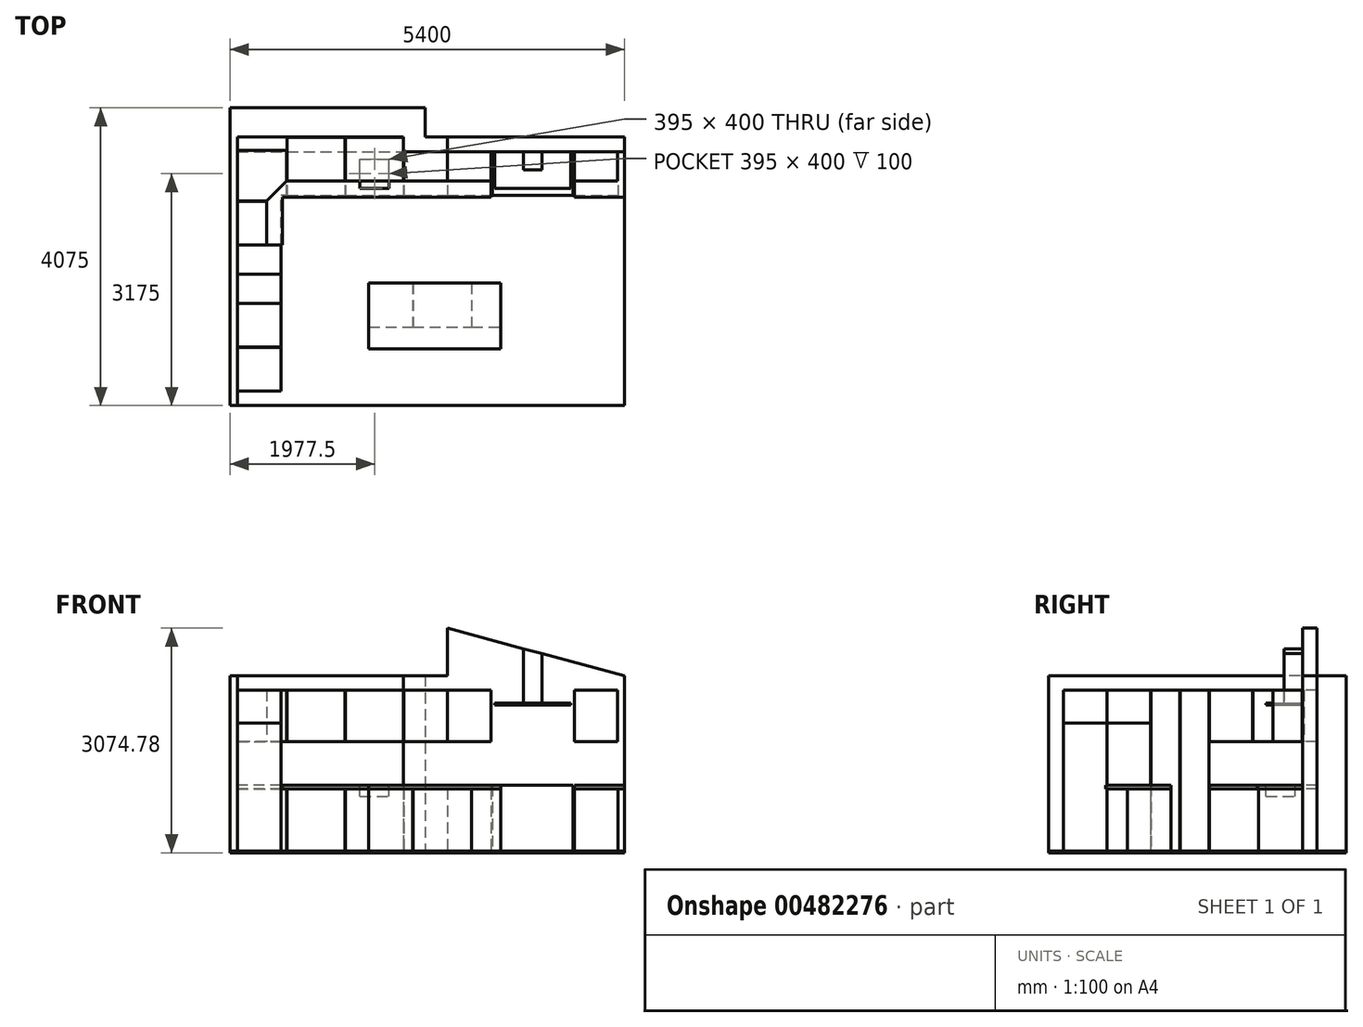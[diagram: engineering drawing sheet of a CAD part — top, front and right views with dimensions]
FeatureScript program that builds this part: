
annotation { "Feature Type Name" : "Feature", "Feature Type Description" : "" }
export const myFeature = defineFeature(function(context is Context, id is Id, definition is map)
    precondition{}
    {
        {
            var Q0;
            Q0=qCreatedBy(makeId("Top.planeOp"),FACE);
            var sketch = newSketch(context, id + "F0", { "sketchPlane" : qUnion([Q0])});
            skLineSegment(sketch, "E0", {"start": v(0, 200) * mm, "end": v(0, -3475) * mm});
            skLineSegment(sketch, "E1", {"start": v(0, 200) * mm, "end": v(2275, 200) * mm});
            skLineSegment(sketch, "E2", {"start": v(2275, 200) * mm, "end": v(2275, 0) * mm});
            skLineSegment(sketch, "E3", {"start": v(2275, 0) * mm, "end": v(5300, 0) * mm});
            skLineSegment(sketch, "E4", {"start": v(0, -3475) * mm, "end": v(-100, -3475) * mm});
            skLineSegment(sketch, "E5", {"start": v(-100, -3475) * mm, "end": v(-100, 600) * mm});
            skLineSegment(sketch, "E6", {"start": v(-100, 600) * mm, "end": v(2575, 600) * mm});
            skLineSegment(sketch, "E7", {"start": v(2575, 600) * mm, "end": v(2575, 200) * mm});
            skLineSegment(sketch, "E8", {"start": v(2575, 200) * mm, "end": v(5300, 200) * mm});
            skLineSegment(sketch, "E9", {"start": v(5300, 200) * mm, "end": v(5300, 0) * mm});
            skLineSegment(sketch, "E10", {"start": v(0, -3475) * mm, "end": v(5300, -3475) * mm});
            skLineSegment(sketch, "E11", {"start": v(5300, -3475) * mm, "end": v(5300, 0) * mm});
            skSolve(sketch);
        }
        {
            var Q0;
            Q0=makeQuery(id+"F0.imprint","IMPRINT",FACE,{"disambiguationData":[TD([[makeQuery(id+"F0.imprint","IMPRINT",EDGE,{"derivedFrom":sQuery(id+"F0.wireOp",EDGE,"E0")}),-1.0]])]});
            extrude(context, id + "F1", {"entities" : qUnion([Q0]), "depth" : 2400 * mm});
        }
        {
            var Q0;
            Q0=qCreatedBy(makeId("Top.planeOp"),FACE);
            var sketch = newSketch(context, id + "F2", { "sketchPlane" : qUnion([Q0])});
            skLineSegment(sketch, "E12", {"start": v(0, 0) * mm, "end": v(675, 0) * mm});
            skLineSegment(sketch, "E13", {"start": v(675, -600) * mm, "end": v(675, 0) * mm});
            skLineSegment(sketch, "E14", {"start": v(675, -600) * mm, "end": v(600, -600) * mm});
            skLineSegment(sketch, "E15", {"start": v(600, -1275) * mm, "end": v(600, -600) * mm});
            skLineSegment(sketch, "E16", {"start": v(600, -1275) * mm, "end": v(0, -1275) * mm});
            skLineSegment(sketch, "E17", {"start": v(0, 0) * mm, "end": v(0, -1275) * mm});
            skLineSegment(sketch, "E18.bottom", {"start": v(680, 0) * mm, "end": v(1475, 0) * mm});
            skLineSegment(sketch, "E18.top", {"start": v(680, -600) * mm, "end": v(1475, -600) * mm});
            skLineSegment(sketch, "E18.left", {"start": v(680, 0) * mm, "end": v(680, -600) * mm});
            skLineSegment(sketch, "E18.right", {"start": v(1475, 0) * mm, "end": v(1475, -600) * mm});
            skLineSegment(sketch, "E19.bottom", {"start": v(1480, 0) * mm, "end": v(2275, 0) * mm});
            skLineSegment(sketch, "E19.top", {"start": v(1480, -600) * mm, "end": v(2275, -600) * mm});
            skLineSegment(sketch, "E19.left", {"start": v(1480, 0) * mm, "end": v(1480, -600) * mm});
            skLineSegment(sketch, "E19.right", {"start": v(2275, 0) * mm, "end": v(2275, -600) * mm});
            skLineSegment(sketch, "E20.bottom", {"start": v(2280, 0) * mm, "end": v(2875, 0) * mm});
            skLineSegment(sketch, "E20.top", {"start": v(2280, -600) * mm, "end": v(2875, -600) * mm});
            skLineSegment(sketch, "E20.left", {"start": v(2280, 0) * mm, "end": v(2280, -600) * mm});
            skLineSegment(sketch, "E20.right", {"start": v(2875, 0) * mm, "end": v(2875, -600) * mm});
            skLineSegment(sketch, "E21.bottom", {"start": v(2880, 0) * mm, "end": v(3475, 0) * mm});
            skLineSegment(sketch, "E21.top", {"start": v(2880, -600) * mm, "end": v(3475, -600) * mm});
            skLineSegment(sketch, "E21.left", {"start": v(2880, 0) * mm, "end": v(2880, -600) * mm});
            skLineSegment(sketch, "E21.right", {"start": v(3475, 0) * mm, "end": v(3475, -600) * mm});
            skLineSegment(sketch, "E22.bottom", {"start": v(3495, 0) * mm, "end": v(4595, 0) * mm});
            skLineSegment(sketch, "E22.top", {"start": v(3495, -600) * mm, "end": v(4595, -600) * mm});
            skLineSegment(sketch, "E22.left", {"start": v(3495, 0) * mm, "end": v(3495, -600) * mm});
            skLineSegment(sketch, "E22.right", {"start": v(4595, 0) * mm, "end": v(4595, -600) * mm});
            skLineSegment(sketch, "E23.bottom", {"start": v(4615, 0) * mm, "end": v(5215, 0) * mm});
            skLineSegment(sketch, "E23.top", {"start": v(4615, -600) * mm, "end": v(5215, -600) * mm});
            skLineSegment(sketch, "E23.left", {"start": v(4615, 0) * mm, "end": v(4615, -600) * mm});
            skLineSegment(sketch, "E23.right", {"start": v(5215, 0) * mm, "end": v(5215, -600) * mm});
            skSolve(sketch);
        }
        {
            var Q0;
            Q0=makeQuery(id+"F2.imprint","IMPRINT",FACE,{"disambiguationData":[TD([[makeQuery(id+"F2.imprint","IMPRINT",EDGE,{"derivedFrom":sQuery(id+"F2.wireOp",EDGE,"E12")}),1.0]])]});
            var Q1;
            Q1=makeQuery(id+"F2.imprint","IMPRINT",FACE,{"disambiguationData":[TD([[makeQuery(id+"F2.imprint","IMPRINT",EDGE,{"derivedFrom":sQuery(id+"F2.wireOp",EDGE,"E12")}),-1.0]])]});
            extrude(context, id + "F3", {"entities" : qUnion([Q0, Q1]), "depth" : 850 * mm});
        }
        {
            var Q0;
            Q0=qCreatedBy(makeId("Top.planeOp"),FACE);
            var sketch = newSketch(context, id + "F4", { "sketchPlane" : qUnion([Q0])});
            skLineSegment(sketch, "E24.bottom", {"start": v(0, -1280) * mm, "end": v(600, -1280) * mm});
            skLineSegment(sketch, "E24.top", {"start": v(0, -2075) * mm, "end": v(600, -2075) * mm});
            skLineSegment(sketch, "E24.left", {"start": v(0, -1280) * mm, "end": v(0, -1675) * mm});
            skLineSegment(sketch, "E24.right", {"start": v(600, -1280) * mm, "end": v(600, -1675) * mm});
            skLineSegment(sketch, "E25.bottom", {"start": v(0, -2080) * mm, "end": v(600, -2080) * mm});
            skLineSegment(sketch, "E25.top", {"start": v(0, -2675) * mm, "end": v(600, -2675) * mm});
            skLineSegment(sketch, "E25.left", {"start": v(0, -2080) * mm, "end": v(0, -2675) * mm});
            skLineSegment(sketch, "E25.right", {"start": v(600, -2080) * mm, "end": v(600, -2675) * mm});
            skLineSegment(sketch, "E26.bottom", {"start": v(0, -2680) * mm, "end": v(600, -2680) * mm});
            skLineSegment(sketch, "E26.top", {"start": v(0, -3275) * mm, "end": v(600, -3275) * mm});
            skLineSegment(sketch, "E26.left", {"start": v(0, -2680) * mm, "end": v(0, -3275) * mm});
            skLineSegment(sketch, "E26.right", {"start": v(600, -2680) * mm, "end": v(600, -3275) * mm});
            skLineSegment(sketch, "E27", {"start": v(0, -1680) * mm, "end": v(600, -1680) * mm});
            skPoint(sketch, "E27.endSnap0", {"position": v(600, -1677.5) * mm});
            skLineSegment(sketch, "E28", {"start": v(0, -1675) * mm, "end": v(600, -1675) * mm});
            skLineSegment(sketch, "E29.trimOffspring", {"start": v(0, -1680) * mm, "end": v(0, -2075) * mm});
            skLineSegment(sketch, "E30.trimOffspring", {"start": v(600, -1680) * mm, "end": v(600, -2075) * mm});
            skSolve(sketch);
        }
        {
            var Q0;
            Q0=makeQuery(id+"F4.imprint","IMPRINT",FACE,{"disambiguationData":[TD([[makeQuery(id+"F4.imprint","IMPRINT",EDGE,{"derivedFrom":sQuery(id+"F4.wireOp",EDGE,"xJVdDzhz-qRA4-ksoh-fODy-tzABdkis1T4j.bottom")}),-1.0]])]});
            var Q1;
            Q1=makeQuery(id+"F4.imprint","IMPRINT",FACE,{"disambiguationData":[TD([[makeQuery(id+"F4.imprint","IMPRINT",EDGE,{"derivedFrom":sQuery(id+"F4.wireOp",EDGE,"E24.bottom")}),-1.0]])]});
            extrude(context, id + "F5", {"entities" : qUnion([Q0, Q1]), "depth" : 2200 * mm});
        }
        {
            var Q0;
            Q0=makeQuery(id+"F4.imprint","IMPRINT",FACE,{"disambiguationData":[TD([[makeQuery(id+"F4.imprint","IMPRINT",EDGE,{"derivedFrom":sQuery(id+"F4.wireOp",EDGE,"E24.top")}),1.0]])]});
            extrude(context, id + "F6", {"entities" : qUnion([Q0]), "depth" : 2200 * mm});
        }
        {
            var Q0;
            Q0=makeQuery(id+"F4.imprint","IMPRINT",FACE,{"disambiguationData":[TD([[makeQuery(id+"F4.imprint","IMPRINT",EDGE,{"derivedFrom":sQuery(id+"F4.wireOp",EDGE,"E25.bottom")}),-1.0]])]});
            extrude(context, id + "F7", {"entities" : qUnion([Q0]), "depth" : 1750 * mm});
        }
        {
            var Q0;
            Q0=makeQuery(id+"F4.imprint","IMPRINT",FACE,{"disambiguationData":[TD([[makeQuery(id+"F4.imprint","IMPRINT",EDGE,{"derivedFrom":sQuery(id+"F4.wireOp",EDGE,"E26.bottom")}),-1.0]])]});
            extrude(context, id + "F8", {"entities" : qUnion([Q0]), "depth" : 1750 * mm});
        }
        {
            var Q0;
            Q0=makeQuery(id+"F2.imprint","IMPRINT",FACE,{"disambiguationData":[TD([[makeQuery(id+"F2.imprint","IMPRINT",EDGE,{"derivedFrom":sQuery(id+"F2.wireOp",EDGE,"E18.bottom")}),-1.0]])]});
            extrude(context, id + "F9", {"entities" : qUnion([Q0]), "depth" : 850 * mm});
        }
        {
            var Q0;
            Q0=makeQuery(id+"F2.imprint","IMPRINT",FACE,{"disambiguationData":[TD([[makeQuery(id+"F2.imprint","IMPRINT",EDGE,{"derivedFrom":sQuery(id+"F2.wireOp",EDGE,"E19.bottom")}),-1.0]])]});
            extrude(context, id + "F10", {"entities" : qUnion([Q0]), "depth" : 850 * mm});
        }
        {
            var Q0;
            Q0=makeQuery(id+"F2.imprint","IMPRINT",FACE,{"disambiguationData":[TD([[makeQuery(id+"F2.imprint","IMPRINT",EDGE,{"derivedFrom":sQuery(id+"F2.wireOp",EDGE,"E20.bottom")}),-1.0]])]});
            extrude(context, id + "F11", {"entities" : qUnion([Q0]), "depth" : 850 * mm});
        }
        {
            var Q0;
            Q0=makeQuery(id+"F2.imprint","IMPRINT",FACE,{"disambiguationData":[TD([[makeQuery(id+"F2.imprint","IMPRINT",EDGE,{"derivedFrom":sQuery(id+"F2.wireOp",EDGE,"E21.bottom")}),-1.0]])]});
            extrude(context, id + "F12", {"entities" : qUnion([Q0]), "depth" : 850 * mm});
        }
        {
            var Q0;
            Q0=makeQuery(id+"F2.imprint","IMPRINT",FACE,{"disambiguationData":[TD([[makeQuery(id+"F2.imprint","IMPRINT",EDGE,{"derivedFrom":sQuery(id+"F2.wireOp",EDGE,"E22.bottom")}),-1.0]])]});
            extrude(context, id + "F13", {"entities" : qUnion([Q0]), "depth" : 900 * mm});
        }
        {
            var Q0;
            Q0=makeQuery(id+"F2.imprint","IMPRINT",FACE,{"disambiguationData":[TD([[makeQuery(id+"F2.imprint","IMPRINT",EDGE,{"derivedFrom":sQuery(id+"F2.wireOp",EDGE,"E23.bottom")}),-1.0]])]});
            extrude(context, id + "F14", {"entities" : qUnion([Q0]), "depth" : 850 * mm});
        }
        {
            var Q0;
            Q0=qCreatedBy(makeId("Top.planeOp"),FACE);
            cPlane(context, id + "F15", {"entities" : qUnion([Q0]), "cplaneType" : CPlaneType.OFFSET, "offset" : 1500 * mm, "width" : 150 * mm, "height" : 150 * mm});
        }
        {
            var Q0;
            Q0=qCreatedBy(id+"F15.planeOp",FACE);
            var sketch = newSketch(context, id + "F16", { "sketchPlane" : qUnion([Q0])});
            skLineSegment(sketch, "E31.bottom", {"start": v(1, 199) * mm, "end": v(675, 199) * mm});
            skLineSegment(sketch, "E31.left", {"start": v(1, 199) * mm, "end": v(1, -676) * mm});
            skLineSegment(sketch, "E31.right", {"start": v(675, 199) * mm, "end": v(675, -401) * mm});
            skPoint(sketch, "E32.0", {"position": v(0, 200) * mm});
            skLineSegment(sketch, "E33.bottom", {"start": v(680, 199) * mm, "end": v(1475, 199) * mm});
            skLineSegment(sketch, "E33.top", {"start": v(680, -401) * mm, "end": v(1475, -401) * mm});
            skLineSegment(sketch, "E33.left", {"start": v(680, 199) * mm, "end": v(680, -401) * mm});
            skLineSegment(sketch, "E33.right", {"start": v(1475, 199) * mm, "end": v(1475, -401) * mm});
            skLineSegment(sketch, "E34.bottom", {"start": v(1480, 199) * mm, "end": v(2275, 199) * mm});
            skLineSegment(sketch, "E34.top", {"start": v(1480, -401) * mm, "end": v(2275, -401) * mm});
            skLineSegment(sketch, "E34.left", {"start": v(1480, 199) * mm, "end": v(1480, -401) * mm});
            skLineSegment(sketch, "E34.right", {"start": v(2275, 199) * mm, "end": v(2275, -401) * mm});
            skLineSegment(sketch, "E35.bottom", {"start": v(2280, -401) * mm, "end": v(2875, -401) * mm});
            skLineSegment(sketch, "E35.top", {"start": v(2280, -1) * mm, "end": v(2875, -1) * mm});
            skLineSegment(sketch, "E35.left", {"start": v(2280, -401) * mm, "end": v(2280, -1) * mm});
            skLineSegment(sketch, "E35.right", {"start": v(2875, -401) * mm, "end": v(2875, -1) * mm});
            skLineSegment(sketch, "E36.bottom", {"start": v(2880, -401) * mm, "end": v(3475, -401) * mm});
            skLineSegment(sketch, "E36.top", {"start": v(2880, -1) * mm, "end": v(3475, -1) * mm});
            skLineSegment(sketch, "E36.left", {"start": v(2880, -401) * mm, "end": v(2880, -1) * mm});
            skLineSegment(sketch, "E36.right", {"start": v(3475, -401) * mm, "end": v(3475, -1) * mm});
            skLineSegment(sketch, "E37.bottom", {"start": v(4615, -401) * mm, "end": v(5210, -401) * mm});
            skLineSegment(sketch, "E37.top", {"start": v(4615, -1) * mm, "end": v(5210, -1) * mm});
            skLineSegment(sketch, "E37.left", {"start": v(4615, -401) * mm, "end": v(4615, -1) * mm});
            skLineSegment(sketch, "E37.right", {"start": v(5210, -401) * mm, "end": v(5210, -1) * mm});
            skLineSegment(sketch, "E38", {"start": v(675, -401) * mm, "end": v(401, -676) * mm});
            skLineSegment(sketch, "E39", {"start": v(401, -676) * mm, "end": v(1, -676) * mm});
            skLineSegment(sketch, "E40.bottom", {"start": v(1, -681) * mm, "end": v(401, -681) * mm});
            skLineSegment(sketch, "E40.top", {"start": v(1, -1276) * mm, "end": v(401, -1276) * mm});
            skLineSegment(sketch, "E40.left", {"start": v(1, -681) * mm, "end": v(1, -1276) * mm});
            skLineSegment(sketch, "E40.right", {"start": v(401, -681) * mm, "end": v(401, -1276) * mm});
            skLineSegment(sketch, "E41", {"start": v(1, 18.87) * mm, "end": v(675, 18.87) * mm});
            skSolve(sketch);
        }
        {
            var Q0;
            Q0=makeQuery(id+"F16.imprint","IMPRINT",FACE,{"disambiguationData":[TD([[makeQuery(id+"F16.imprint","IMPRINT",EDGE,{"derivedFrom":sQuery(id+"F16.wireOp",EDGE,"E33.bottom")}),-1.0]])]});
            extrude(context, id + "F17", {"entities" : qUnion([Q0]), "depth" : 700 * mm});
        }
        {
            var Q0;
            Q0=makeQuery(id+"F16.imprint","IMPRINT",FACE,{"disambiguationData":[TD([[makeQuery(id+"F16.imprint","IMPRINT",EDGE,{"derivedFrom":sQuery(id+"F16.wireOp",EDGE,"E34.bottom")}),-1.0]])]});
            extrude(context, id + "F18", {"entities" : qUnion([Q0]), "depth" : 700 * mm});
        }
        {
            var Q0;
            Q0=makeQuery(id+"F0.imprint","IMPRINT",FACE,{"disambiguationData":[TD([[makeQuery(id+"F0.imprint","IMPRINT",EDGE,{"derivedFrom":sQuery(id+"F0.wireOp",EDGE,"E0")}),-1.0]])]});
            var Q1;
            Q1=makeQuery(id+"F0.imprint","IMPRINT",FACE,{"disambiguationData":[TD([[makeQuery(id+"F0.imprint","IMPRINT",EDGE,{"derivedFrom":sQuery(id+"F0.wireOp",EDGE,"E0")}),1.0]])]});
            extrude(context, id + "F19", {"entities" : qUnion([Q0, Q1]), "oppositeDirection" : true, "depth" : 25 * mm});
        }
        {
            var Q0;
            Q0=makeQuery(id+"F16.imprint","IMPRINT",FACE,{"disambiguationData":[TD([[makeQuery(id+"F16.imprint","IMPRINT",EDGE,{"derivedFrom":sQuery(id+"F16.wireOp",EDGE,"E35.bottom")}),1.0]])]});
            var Q1;
            Q1=makeQuery(id+"F16.imprint","IMPRINT",FACE,{"disambiguationData":[TD([[makeQuery(id+"F16.imprint","IMPRINT",EDGE,{"derivedFrom":sQuery(id+"F16.wireOp",EDGE,"E36.bottom")}),1.0]])]});
            var Q2;
            Q2=makeQuery(id+"F16.imprint","IMPRINT",FACE,{"disambiguationData":[TD([[makeQuery(id+"F16.imprint","IMPRINT",EDGE,{"derivedFrom":sQuery(id+"F16.wireOp",EDGE,"E37.bottom")}),1.0]])]});
            extrude(context, id + "F20", {"entities" : qUnion([Q0, Q1, Q2]), "depth" : 700 * mm});
        }
        {
            var Q0;
            Q0=makeQuery(id+"F1.opExtrude","SWEPT_FACE",FACE,{"disambiguationData":[OSD([sQuery(id+"F0.wireOp",EDGE,"E3")])]});
            var sketch = newSketch(context, id + "F21", { "sketchPlane" : qUnion([Q0])});
            skLineSegment(sketch, "E42", {"start": v(5300, 2400) * mm, "end": v(2875, 3049.78) * mm});
            skLineSegment(sketch, "E43", {"start": v(2875, 3049.78) * mm, "end": v(2875, 2400) * mm});
            skLineSegment(sketch, "E44", {"start": v(2875, 2400) * mm, "end": v(5300, 2400) * mm});
            skLineSegment(sketch, "E45.0", {"start": v(2575, 2400) * mm, "end": v(2575, 0) * mm});
            skSolve(sketch);
        }
        {
            var Q0;
            Q0=makeQuery(id+"F21.imprint","IMPRINT",FACE,{"disambiguationData":[TD([[makeQuery(id+"F21.imprint","IMPRINT",EDGE,{"derivedFrom":sQuery(id+"F21.wireOp",EDGE,"E42")}),1.0]])]});
            extrude(context, id + "F22", {"entities" : qUnion([Q0]), "operationType" : NewBodyOperationType.ADD, "oppositeDirection" : true, "depth" : 200 * mm});
        }
        {
            var Q0;
            Q0=makeQuery(id+"F22.boolean.opBoolean","MERGE",FACE,{"derivedFrom":[makeQuery(id+"F1.opExtrude","SWEPT_FACE",FACE,{"disambiguationData":[OSD([sQuery(id+"F0.wireOp",EDGE,"E3")])]}),makeQuery(id+"F22.opExtrude","CAP_FACE",FACE,{"disambiguationData":[OSD([sQuery(id+"F21.wireOp",EDGE,"E42"),sQuery(id+"F21.wireOp",EDGE,"E43"),sQuery(id+"F21.wireOp",EDGE,"E44")])],"isStart":true})]});
            var sketch = newSketch(context, id + "F23", { "sketchPlane" : qUnion([Q0])});
            skLineSegment(sketch, "E46.bottom", {"start": v(3525, 2000) * mm, "end": v(4565, 2000) * mm});
            skLineSegment(sketch, "E46.top", {"start": v(3525, 2025) * mm, "end": v(3920, 2025) * mm});
            skLineSegment(sketch, "E46.left", {"start": v(3525, 2000) * mm, "end": v(3525, 2025) * mm});
            skLineSegment(sketch, "E46.right", {"start": v(4565, 2000) * mm, "end": v(4565, 2025) * mm});
            skLineSegment(sketch, "E47", {"start": v(3920, 2025) * mm, "end": v(3920, 2769.77) * mm});
            skLineSegment(sketch, "E48", {"start": v(3920, 2769.77) * mm, "end": v(4170, 2702.78) * mm});
            skLineSegment(sketch, "E49", {"start": v(4170, 2702.78) * mm, "end": v(4170, 2025) * mm});
            skLineSegment(sketch, "E50.trimOffspring", {"start": v(4170, 2025) * mm, "end": v(4565, 2025) * mm});
            skLineSegment(sketch, "E51", {"start": v(3920, 2025) * mm, "end": v(4170, 2025) * mm});
            skSolve(sketch);
        }
        {
            var Q0;
            Q0=makeQuery(id+"F23.imprint","IMPRINT",FACE,{"disambiguationData":[TD([[makeQuery(id+"F23.imprint","IMPRINT",EDGE,{"derivedFrom":sQuery(id+"F23.wireOp",EDGE,"E47")}),-1.0]])]});
            extrude(context, id + "F24", {"entities" : qUnion([Q0]), "depth" : 250 * mm});
        }
        {
            var Q0;
            Q0=makeQuery(id+"F23.imprint","IMPRINT",FACE,{"disambiguationData":[TD([[makeQuery(id+"F23.imprint","IMPRINT",EDGE,{"derivedFrom":sQuery(id+"F23.wireOp",EDGE,"E46.bottom")}),1.0]])]});
            extrude(context, id + "F25", {"entities" : qUnion([Q0]), "depth" : 500 * mm});
        }
        {
            var Q0;
            {var subQ1=sQuery(id+"F16.wireOp",EDGE,"E38");Q0=makeQuery(id+"F16.imprint","IMPRINT",FACE,{"disambiguationData":[TD([[makeQuery(id+"F16.imprint","IMPRINT",EDGE,{"derivedFrom":subQ1}),-1.0]])]});}
            extrude(context, id + "F26", {"entities" : qUnion([Q0]), "depth" : 700 * mm});
        }
        {
            var Q0;
            Q0=makeQuery(id+"F16.imprint","IMPRINT",FACE,{"disambiguationData":[TD([[makeQuery(id+"F16.imprint","IMPRINT",EDGE,{"derivedFrom":sQuery(id+"F16.wireOp",EDGE,"E40.bottom")}),-1.0]])]});
            extrude(context, id + "F27", {"entities" : qUnion([Q0]), "depth" : 700 * mm});
        }
        {
            var Q0;
            Q0=makeQuery(id+"F10.opExtrude","CAP_FACE",FACE,{"disambiguationData":[OSD([sQuery(id+"F2.wireOp",EDGE,"E19.bottom"),sQuery(id+"F2.wireOp",EDGE,"E19.top"),sQuery(id+"F2.wireOp",EDGE,"E19.left"),sQuery(id+"F2.wireOp",EDGE,"E19.right")])],"isStart":false});
            var sketch = newSketch(context, id + "F28", { "sketchPlane" : qUnion([Q0])});
            skLineSegment(sketch, "E52.bottom", {"start": v(1680, -500) * mm, "end": v(2075, -500) * mm});
            skLineSegment(sketch, "E52.top", {"start": v(1680, -100) * mm, "end": v(2075, -100) * mm});
            skLineSegment(sketch, "E52.left", {"start": v(1680, -500) * mm, "end": v(1680, -100) * mm});
            skLineSegment(sketch, "E52.right", {"start": v(2075, -500) * mm, "end": v(2075, -100) * mm});
            skSolve(sketch);
        }
        {
            var Q0;
            Q0=makeQuery(id+"F19.opExtrude","CAP_FACE",FACE,{"disambiguationData":[OSD([sQuery(id+"F0.wireOp",EDGE,"E4"),sQuery(id+"F0.wireOp",EDGE,"E5"),sQuery(id+"F0.wireOp",EDGE,"E6"),sQuery(id+"F0.wireOp",EDGE,"E7"),sQuery(id+"F0.wireOp",EDGE,"E8"),sQuery(id+"F0.wireOp",EDGE,"E9"),sQuery(id+"F0.wireOp",EDGE,"E10"),sQuery(id+"F0.wireOp",EDGE,"E11")])],"isStart":true});
            cPlane(context, id + "F29", {"entities" : qUnion([Q0]), "cplaneType" : CPlaneType.OFFSET, "offset" : 851 * mm, "width" : 150 * mm, "height" : 150 * mm});
        }
        {
            var Q0;
            Q0=qCreatedBy(id+"F29.planeOp",FACE);
            var sketch = newSketch(context, id + "F30", { "sketchPlane" : qUnion([Q0])});
            skLineSegment(sketch, "E53.1", {"start": v(0, 200) * mm, "end": v(0, -1274) * mm});
            skLineSegment(sketch, "E53.2", {"start": v(0, 200) * mm, "end": v(2275, 200) * mm});
            skLineSegment(sketch, "E53.3", {"start": v(2275, 200) * mm, "end": v(2275, 0) * mm});
            skLineSegment(sketch, "E53.4", {"start": v(2275, 0) * mm, "end": v(3475, 0) * mm});
            skLineSegment(sketch, "E54.0", {"start": v(5300, 0) * mm, "end": v(5300, -620) * mm});
            skPoint(sketch, "E55.orphan", {"position": v(2875, 0) * mm});
            skPoint(sketch, "E56.orphan", {"position": v(5300, 200) * mm});
            skLineSegment(sketch, "E57", {"start": v(5300, -620) * mm, "end": v(4615, -620) * mm});
            skLineSegment(sketch, "E58", {"start": v(620, -620) * mm, "end": v(620, -1274) * mm});
            skLineSegment(sketch, "E59", {"start": v(620, -1274) * mm, "end": v(0, -1274) * mm});
            skPoint(sketch, "E60.orphan", {"position": v(0, -3475) * mm});
            skPoint(sketch, "E61.orphan", {"position": v(5300, -3475) * mm});
            skLineSegment(sketch, "E62.0", {"start": v(3475, 0) * mm, "end": v(3475, -620) * mm});
            skLineSegment(sketch, "E63.0", {"start": v(4615, 0) * mm, "end": v(4615, -620) * mm});
            skPoint(sketch, "E64.orphan", {"position": v(4615, -600) * mm});
            skPoint(sketch, "E65.orphan", {"position": v(3475, -600) * mm});
            skLineSegment(sketch, "E66.trimOffspring", {"start": v(3475, -620) * mm, "end": v(620, -620) * mm});
            skLineSegment(sketch, "E67.trimOffspring", {"start": v(4615, 0) * mm, "end": v(5300, 0) * mm});
            skSolve(sketch);
        }
        {
            var Q0;
            Q0=makeQuery(id+"F30.imprint","IMPRINT",FACE,{"disambiguationData":[TD([[makeQuery(id+"F30.imprint","IMPRINT",EDGE,{"derivedFrom":sQuery(id+"F30.wireOp",EDGE,"E53.1")}),1.0]])]});
            var Q1;
            Q1=makeQuery(id+"F30.imprint","IMPRINT",FACE,{"disambiguationData":[TD([[makeQuery(id+"F30.imprint","IMPRINT",EDGE,{"derivedFrom":sQuery(id+"F30.wireOp",EDGE,"E54.0")}),-1.0]])]});
            extrude(context, id + "F31", {"entities" : qUnion([Q0, Q1]), "depth" : 50 * mm});
        }
        {
            var Q0;
            Q0=makeQuery(id+"F28.imprint","IMPRINT",FACE,{"disambiguationData":[TD([[makeQuery(id+"F28.imprint","IMPRINT",EDGE,{"derivedFrom":sQuery(id+"F28.wireOp",EDGE,"E52.bottom")}),1.0]])]});
            extrude(context, id + "F32", {"entities" : qUnion([Q0]), "operationType" : NewBodyOperationType.REMOVE, "endBound" : BoundingType.SYMMETRIC, "oppositeDirection" : true, "depth" : 200 * mm});
        }
        {
            var Q0;
            Q0=makeQuery(id+"F5.opExtrude","CAP_FACE",FACE,{"disambiguationData":[OSD([sQuery(id+"F4.wireOp",EDGE,"E24.bottom"),sQuery(id+"F4.wireOp",EDGE,"E24.top"),sQuery(id+"F4.wireOp",EDGE,"E24.left"),sQuery(id+"F4.wireOp",EDGE,"E24.right")])],"isStart":false});
            var sketch = newSketch(context, id + "F33", { "sketchPlane" : qUnion([Q0])});
            skLineSegment(sketch, "E68.bottom", {"start": v(0, -2080) * mm, "end": v(600, -2080) * mm});
            skLineSegment(sketch, "E68.top", {"start": v(0, -2675) * mm, "end": v(600, -2675) * mm});
            skLineSegment(sketch, "E68.left", {"start": v(0, -2080) * mm, "end": v(0, -2675) * mm});
            skLineSegment(sketch, "E68.right", {"start": v(600, -2080) * mm, "end": v(600, -2675) * mm});
            skLineSegment(sketch, "E69.bottom", {"start": v(0, -2680) * mm, "end": v(600, -2680) * mm});
            skLineSegment(sketch, "E69.top", {"start": v(0, -3275) * mm, "end": v(600, -3275) * mm});
            skLineSegment(sketch, "E69.left", {"start": v(0, -2680) * mm, "end": v(0, -3275) * mm});
            skLineSegment(sketch, "E69.right", {"start": v(600, -2680) * mm, "end": v(600, -3275) * mm});
            skSolve(sketch);
        }
        {
            var Q0;
            Q0=makeQuery(id+"F33.imprint","IMPRINT",FACE,{"disambiguationData":[TD([[makeQuery(id+"F33.imprint","IMPRINT",EDGE,{"derivedFrom":sQuery(id+"F33.wireOp",EDGE,"E69.bottom")}),-1.0]])]});
            var Q1;
            Q1=makeQuery(id+"F33.imprint","IMPRINT",FACE,{"disambiguationData":[TD([[makeQuery(id+"F33.imprint","IMPRINT",EDGE,{"derivedFrom":sQuery(id+"F33.wireOp",EDGE,"E68.bottom")}),-1.0]])]});
            extrude(context, id + "F34", {"entities" : qUnion([Q0, Q1]), "oppositeDirection" : true, "depth" : 449 * mm});
        }
        {
            var Q0;
            Q0=makeQuery(id+"F19.opExtrude","CAP_FACE",FACE,{"disambiguationData":[OSD([sQuery(id+"F0.wireOp",EDGE,"E4"),sQuery(id+"F0.wireOp",EDGE,"E5"),sQuery(id+"F0.wireOp",EDGE,"E6"),sQuery(id+"F0.wireOp",EDGE,"E7"),sQuery(id+"F0.wireOp",EDGE,"E8"),sQuery(id+"F0.wireOp",EDGE,"E9"),sQuery(id+"F0.wireOp",EDGE,"E10"),sQuery(id+"F0.wireOp",EDGE,"E11")])],"isStart":true});
            var sketch = newSketch(context, id + "F35", { "sketchPlane" : qUnion([Q0])});
            skLineSegment(sketch, "E70.bottom", {"start": v(1800, -1800) * mm, "end": v(2400, -1800) * mm});
            skLineSegment(sketch, "E70.top", {"start": v(1800, -2400) * mm, "end": v(2400, -2400) * mm});
            skLineSegment(sketch, "E70.left", {"start": v(1800, -1800) * mm, "end": v(1800, -2400) * mm});
            skLineSegment(sketch, "E70.right", {"start": v(2400, -1800) * mm, "end": v(2400, -2400) * mm});
            skLineSegment(sketch, "E71.bottom", {"start": v(2405, -1800) * mm, "end": v(3205, -1800) * mm});
            skLineSegment(sketch, "E71.top", {"start": v(2405, -2400) * mm, "end": v(3205, -2400) * mm});
            skLineSegment(sketch, "E71.left", {"start": v(2405, -1800) * mm, "end": v(2405, -2400) * mm});
            skLineSegment(sketch, "E71.right", {"start": v(3205, -1800) * mm, "end": v(3205, -2400) * mm});
            skLineSegment(sketch, "E72.bottom", {"start": v(3210, -1800) * mm, "end": v(3610, -1800) * mm});
            skLineSegment(sketch, "E72.top", {"start": v(3210, -2400) * mm, "end": v(3610, -2400) * mm});
            skLineSegment(sketch, "E72.left", {"start": v(3210, -1800) * mm, "end": v(3210, -2400) * mm});
            skLineSegment(sketch, "E72.right", {"start": v(3610, -1800) * mm, "end": v(3610, -2400) * mm});
            skSolve(sketch);
        }
        {
            var Q0;
            Q0=makeQuery(id+"F35.imprint","IMPRINT",FACE,{"disambiguationData":[TD([[makeQuery(id+"F35.imprint","IMPRINT",EDGE,{"derivedFrom":sQuery(id+"F35.wireOp",EDGE,"E70.bottom")}),-1.0]])]});
            var Q1;
            Q1=makeQuery(id+"F35.imprint","IMPRINT",FACE,{"disambiguationData":[TD([[makeQuery(id+"F35.imprint","IMPRINT",EDGE,{"derivedFrom":sQuery(id+"F35.wireOp",EDGE,"E71.bottom")}),-1.0]])]});
            var Q2;
            Q2=makeQuery(id+"F35.imprint","IMPRINT",FACE,{"disambiguationData":[TD([[makeQuery(id+"F35.imprint","IMPRINT",EDGE,{"derivedFrom":sQuery(id+"F35.wireOp",EDGE,"E72.bottom")}),-1.0]])]});
            extrude(context, id + "F36", {"entities" : qUnion([Q0, Q1, Q2]), "depth" : 850 * mm});
        }
        {
            var Q0;
            Q0=makeQuery(id+"F36.opExtrude","CAP_FACE",FACE,{"disambiguationData":[OSD([sQuery(id+"F35.wireOp",EDGE,"E70.bottom"),sQuery(id+"F35.wireOp",EDGE,"E70.top"),sQuery(id+"F35.wireOp",EDGE,"E70.left"),sQuery(id+"F35.wireOp",EDGE,"E70.right")])],"isStart":false});
            var sketch = newSketch(context, id + "F37", { "sketchPlane" : qUnion([Q0])});
            skLineSegment(sketch, "E73.bottom", {"start": v(1800, -1800) * mm, "end": v(3610, -1800) * mm});
            skLineSegment(sketch, "E73.top", {"start": v(1800, -2700) * mm, "end": v(3610, -2700) * mm});
            skLineSegment(sketch, "E73.left", {"start": v(1800, -1800) * mm, "end": v(1800, -2700) * mm});
            skLineSegment(sketch, "E73.right", {"start": v(3610, -1800) * mm, "end": v(3610, -2700) * mm});
            skSolve(sketch);
        }
        {
            var Q0;
            {var subQ2=sQuery(id+"F37.wireOp",EDGE,"E73.top");Q0=makeQuery(id+"F37.imprint","IMPRINT",FACE,{"disambiguationData":[TD([[makeQuery(id+"F37.imprint","IMPRINT",EDGE,{"derivedFrom":subQ2}),1.0]])]});}
            var Q1;
            {var subQ4=makeQuery(id+"F36.opExtrude","CAP_EDGE",EDGE,{"disambiguationData":[OSD([sQuery(id+"F35.wireOp",EDGE,"E70.top")])],"isStart":false});Q1=makeQuery(id+"F37.imprint","IMPRINT",FACE,{"disambiguationData":[TD([[makeQuery(id+"F37.imprint","IMPRINT",EDGE,{"derivedFrom":subQ4}),1.0]])]});}
            extrude(context, id + "F38", {"entities" : qUnion([Q0, Q1]), "depth" : 50 * mm});
        }
    });
